# Revit family: Sink-Kitchen-KOHLER-Undertone-K-3325
name_source: partatom
category: Plumbing Fixtures
revit_build: Autodesk Revit 2015 (Build: 20140606_1530(x64)
units: mm (PartAtom-declared; Revit-internal decimal feet)

## types (2) — shared parameters
ADA Compliant = No
Assembly Code = D2010400
CW Connection = No
Cold Water Inlet = Cold Water Inlet
Date Modified = 07/30/2018
Default Elevation = 36"
Drain Included = No
Finish = Kohler-Metal-NA-Stainless
HW Connection = No
Height = 9 1/2"
Hot Water Inlet = Hot Water Inlet
Length = 23"
Manufacturer = KOHLER Co.
MasterFormat 1995 = 15410
MasterFormat 2004 = 22.41.16
Material = 18-Gauge Stainless Steel
Product Documentation Link = http://www.us.kohler.com
Product Name = Undertone
Product Page URL = http://www.us.kohler.com
URL = https://www.us.kohler.com
Vent Connection = No
Waste Connection = Yes
Waste Water Outlet = Waste Water Outlet
Width = 17 1/2"

## per-type parameters (varying)
| type | Description | Model | Type |
| NA-Stainless Steel | 23inch x 17-1/2inch x 9-1/2inch medium squared under-mount single-bowl kitchen sink | K-3325-NA | 1 |
| Preserve, NA-Stainless Steel | Preserve 23inch x 17-1/2inch x 9-1/2inch medium under-mount single-bowl kitchen sink | K-3325-HCF-NA | 2 |

## geometry (parser evidence)
native form markers: Sweep x5
no freeform markers — native parametric forms only
